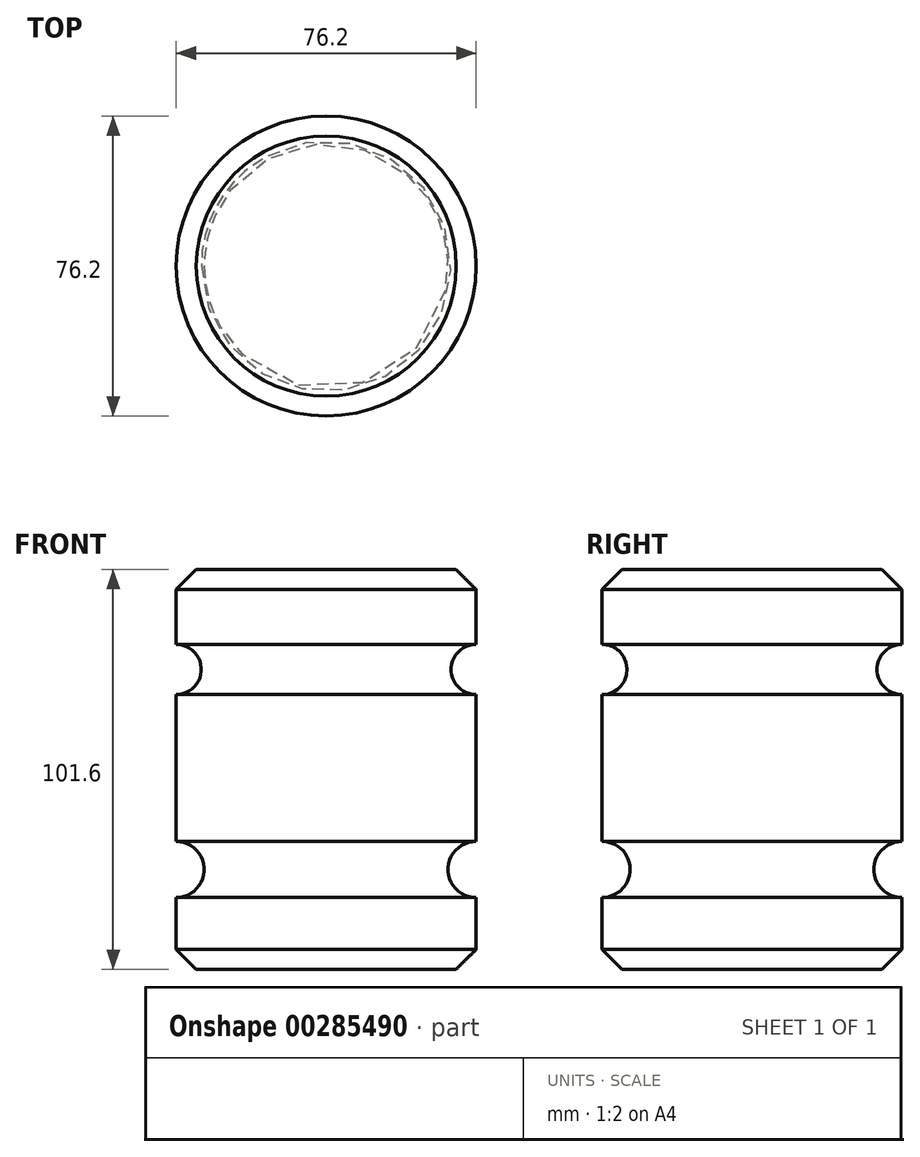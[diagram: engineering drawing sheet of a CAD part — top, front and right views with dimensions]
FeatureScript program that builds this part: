
annotation { "Feature Type Name" : "Feature", "Feature Type Description" : "" }
export const myFeature = defineFeature(function(context is Context, id is Id, definition is map)
    precondition{}
    {
        {
            var Q0;
            Q0=qCreatedBy(makeId("Front.planeOp"),FACE);
            var sketch = newSketch(context, id + "F0", { "sketchPlane" : qUnion([Q0])});
            skLineSegment(sketch, "E0.bottom", {"start": v(0, 0) * mm, "end": v(-38.1, 0) * mm});
            skLineSegment(sketch, "E0.top", {"start": v(0, 101.6) * mm, "end": v(-38.1, 101.6) * mm});
            skLineSegment(sketch, "E0.left", {"start": v(0, 0) * mm, "end": v(0, 18.28) * mm});
            skLineSegment(sketch, "E0.right", {"start": v(-38.1, 0) * mm, "end": v(-38.1, 101.6) * mm});
            skArc(sketch, "E1", {"start": v(0, 82.58) * mm, "mid": v(-6.38, 76.2) * mm, "end": v(0, 69.82) * mm});
            skArc(sketch, "E2", {"start": v(0, 32.52) * mm, "mid": v(-7.12, 25.4) * mm, "end": v(0, 18.28) * mm});
            skLineSegment(sketch, "E3.trimOffspring", {"start": v(0, 82.58) * mm, "end": v(0, 101.6) * mm});
            skLineSegment(sketch, "E4.trimOffspring", {"start": v(0, 32.52) * mm, "end": v(0, 69.82) * mm});
            skSolve(sketch);
        }
        {
            var Q0;
            Q0=qSketchRegion(id+"F0",true);
            var Q1;
            Q1=sQuery(id+"F0.wireOp",EDGE,"E0.right");
            revolve(context, id + "F1", {"entities" : qUnion([Q0]), "axis" : qUnion([Q1]), "revolveType" : RevolveType.FULL});
        }
        {
            var Q0;
            Q0=makeQuery(id+"F1.opRevolve","SWEPT_EDGE",EDGE,{"disambiguationData":[OSD([sQuery(id+"F0.wireOp",EDGE,"E0.top"),sQuery(id+"F0.wireOp",EDGE,"E3.trimOffspring")])]});
            var Q1;
            Q1=makeQuery(id+"F1.opRevolve","SWEPT_EDGE",EDGE,{"disambiguationData":[OSD([sQuery(id+"F0.wireOp",EDGE,"E0.bottom"),sQuery(id+"F0.wireOp",EDGE,"E0.left")])]});
            chamfer(context, id + "F2", {"entities" : qUnion([Q0, Q1]), "width" : 5.08 * mm, "tangentPropagation" : true});
        }
    });
